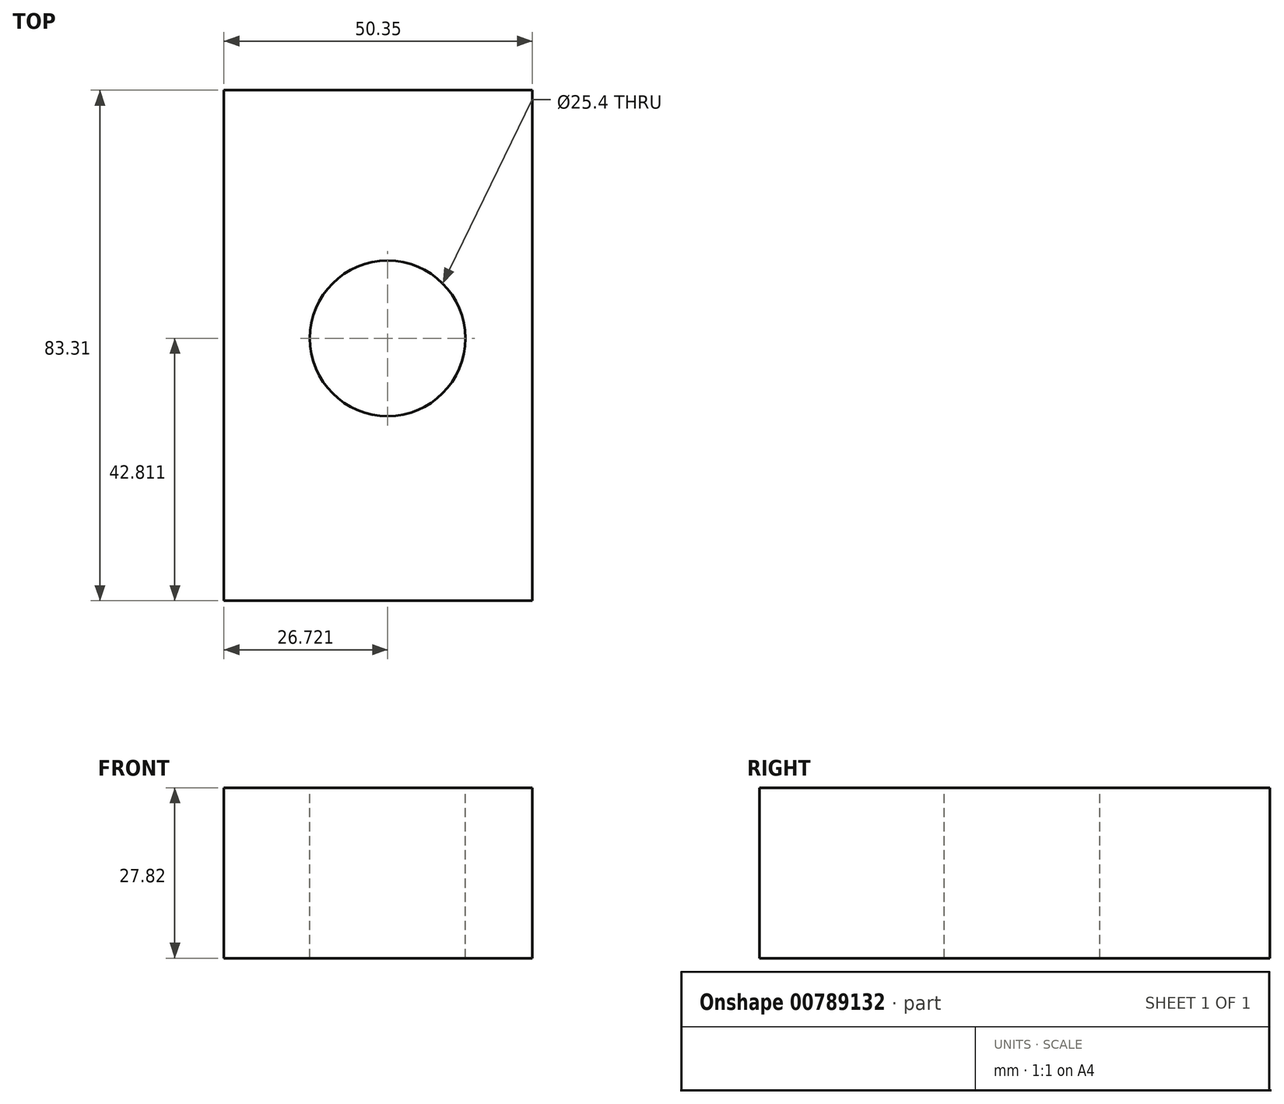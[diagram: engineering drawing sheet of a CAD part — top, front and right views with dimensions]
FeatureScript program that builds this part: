
annotation { "Feature Type Name" : "Feature", "Feature Type Description" : "" }
export const myFeature = defineFeature(function(context is Context, id is Id, definition is map)
    precondition{}
    {
        {
            var Q0;
            Q0=qCreatedBy(makeId("Front.planeOp"),FACE);
            var sketch = newSketch(context, id + "F0", { "sketchPlane" : qUnion([Q0])});
            skLineSegment(sketch, "E0.bottom", {"start": v(0, 0) * mm, "end": v(-50.35, 0) * mm});
            skLineSegment(sketch, "E0.top", {"start": v(0, 27.82) * mm, "end": v(-50.35, 27.82) * mm});
            skLineSegment(sketch, "E0.left", {"start": v(0, 0) * mm, "end": v(0, 27.82) * mm});
            skLineSegment(sketch, "E0.right", {"start": v(-50.35, 0) * mm, "end": v(-50.35, 27.82) * mm});
            skSolve(sketch);
        }
        {
            var Q0;
            Q0=makeQuery(id+"F0.imprint","IMPRINT",FACE,{"disambiguationData":[TD([[makeQuery(id+"F0.imprint","IMPRINT",EDGE,{"derivedFrom":sQuery(id+"F0.wireOp",EDGE,"E0.bottom")}),-1.0]])]});
            extrude(context, id + "F1", {"entities" : qUnion([Q0]), "depth" : 83.31 * mm, "offsetDistance" : 25.4 * mm});
        }
        {
            var Q0;
            Q0=makeQuery(id+"F1.opExtrude","SWEPT_FACE",FACE,{"disambiguationData":[OSD([sQuery(id+"F0.wireOp",EDGE,"E0.top")])]});
            var sketch = newSketch(context, id + "F2", { "sketchPlane" : qUnion([Q0])});
            skCircle(sketch, "E1", {"center": v(-23.63, -40.5) * mm, "radius": 10.5 * mm});
            skSolve(sketch);
        }
        {
            var Q0;
            Q0=sQuery(id+"F2.wireOp",VERTEX,"E1.center");
            var Q1;
            Q1=makeQuery(id+"F1.opExtrude","SWEPT_BODY",BODY,{"disambiguationData":[OSD([sQuery(id+"F0.wireOp",EDGE,"E0.bottom"),sQuery(id+"F0.wireOp",EDGE,"E0.top"),sQuery(id+"F0.wireOp",EDGE,"E0.left"),sQuery(id+"F0.wireOp",EDGE,"E0.right")])]});
            hole(context, id + "F3", {"style" : HoleStyle.SIMPLE, "endStyle" : HoleEndStyle.THROUGH, "holeDiameter" : 25.4 * mm, "majorDiameter" : 6.35 * mm, "isTappedThrough" : true, "tappedDepth" : 12.7 * mm, "tapClearance" : 3, "locations" : qUnion([Q0]), "scope" : qUnion([Q1])});
        }
    });
